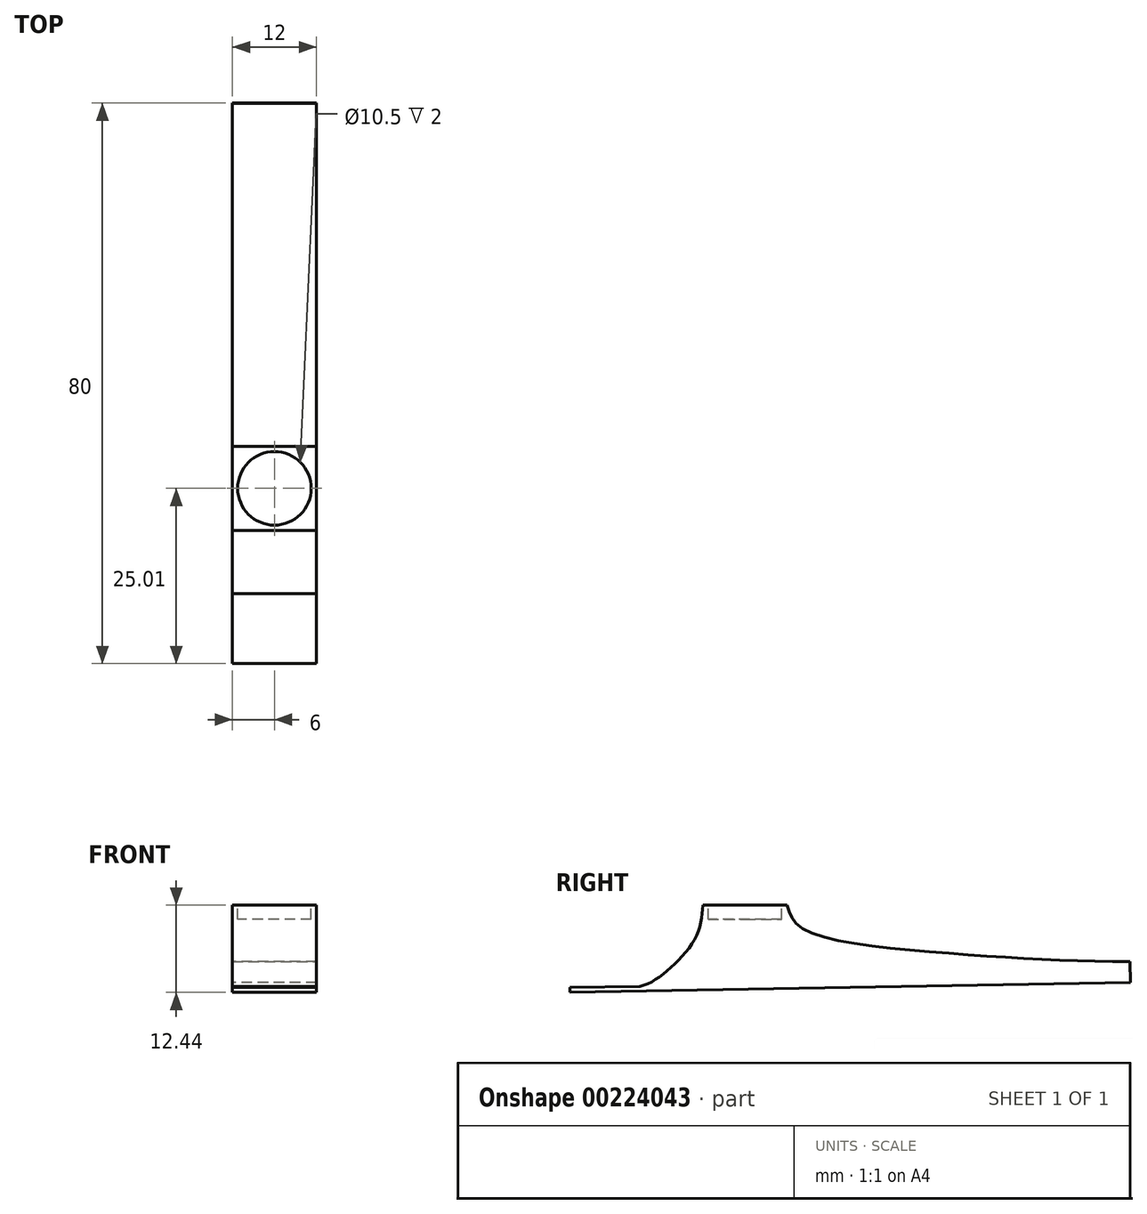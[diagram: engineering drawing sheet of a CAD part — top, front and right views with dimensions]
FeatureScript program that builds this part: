
annotation { "Feature Type Name" : "Feature", "Feature Type Description" : "" }
export const myFeature = defineFeature(function(context is Context, id is Id, definition is map)
    precondition{}
    {
        {
            var Q0;
            Q0=qCreatedBy(makeId("Right.planeOp"),FACE);
            var sketch = newSketch(context, id + "F0", { "sketchPlane" : qUnion([Q0])});
            skLineSegment(sketch, "E0", {"start": v(-6, 0) * mm, "end": v(6, 0) * mm});
            skLineSegment(sketch, "E1", {"start": v(-25, -12.44) * mm, "end": v(54.99, -11.04) * mm});
            skLineSegment(sketch, "E2", {"start": v(-25, -12.44) * mm, "end": v(-25.01, -11.74) * mm});
            skLineSegment(sketch, "E3", {"start": v(-25.01, -11.74) * mm, "end": v(-15.01, -11.56) * mm});
            skPoint(sketch, "E4", {"position": v(0, -12) * mm});
            skFitSpline(sketch, "E5", {"points": [v(-15.01, -11.56) * mm, v(-10.91, -9.17) * mm, v(-6.96, -4.41) * mm, v(-6, 0) * mm], "startDerivative": vector(13.31, 2.48) * mm, "endDerivative": vector(1.31, 13.6) * mm});
            skFitSpline(sketch, "E6", {"points": [v(6, 0) * mm, v(8.1, -3.25) * mm, v(28.89, -6.83) * mm, v(54.97, -8.04) * mm], "startDerivative": vector(6.15, -20.62) * mm, "endDerivative": vector(57.49, 0.33) * mm});
            skLineSegment(sketch, "E7", {"start": v(54.99, -11.04) * mm, "end": v(54.97, -8.04) * mm});
            skSolve(sketch);
        }
        {
            var Q0;
            Q0 = qSketchRegion(id + "F0", true);
            extrude(context, id + "F1", {"entities" : qUnion([Q0]), "depth" : 12 * mm});
        }
        {
            var Q0;
            Q0=makeQuery(id+"F1.opExtrude","SWEPT_FACE",FACE,{"disambiguationData":[OSD([sQuery(id+"F0.wireOp",EDGE,"E0")])]});
            var sketch = newSketch(context, id + "F2", { "sketchPlane" : qUnion([Q0])});
            skCircle(sketch, "E8", {"center": v(6, 0) * mm, "radius": 5.25 * mm});
            skPoint(sketch, "E8.centerSnap0", {"position": v(6, -6) * mm});
            skPoint(sketch, "E8.centerSnap1", {"position": v(12, 0) * mm});
            skSolve(sketch);
        }
        {
            var Q0;
            Q0=makeQuery(id+"F2.imprint","IMPRINT",FACE,{"disambiguationData":[TD([[makeQuery(id+"F2.imprint","IMPRINT",EDGE,{"derivedFrom":sQuery(id+"F2.wireOp",EDGE,"E8")}),1.0]])]});
            extrude(context, id + "F3", {"entities" : qUnion([Q0]), "operationType" : NewBodyOperationType.REMOVE, "oppositeDirection" : true, "depth" : 2 * mm});
        }
    });
